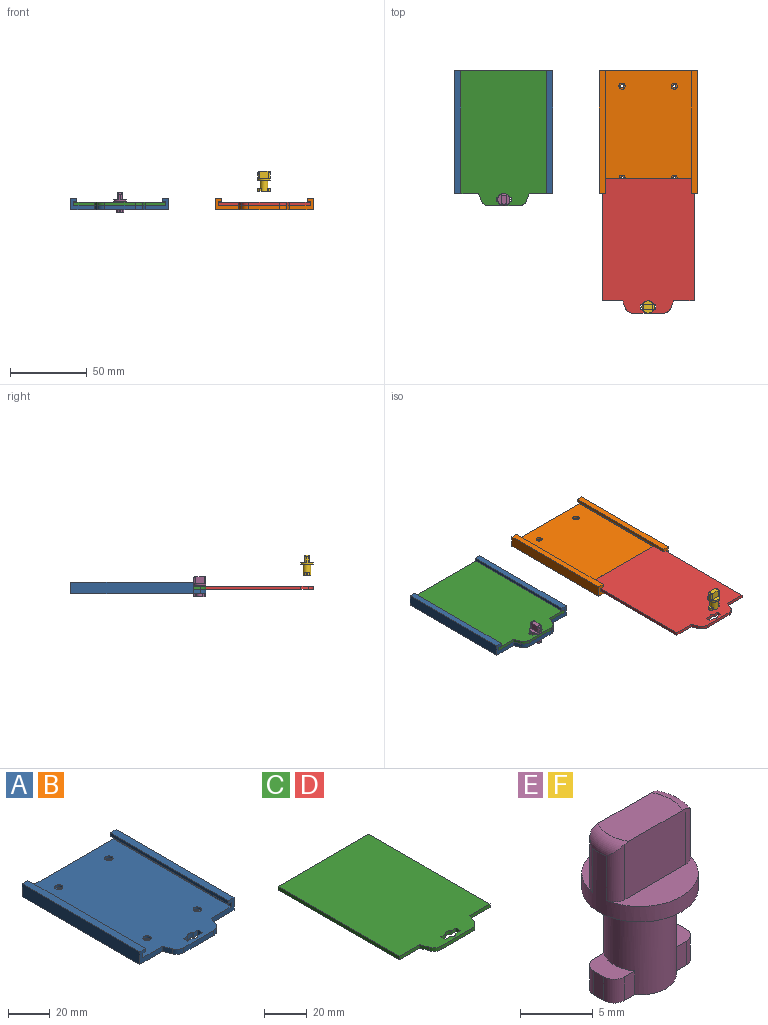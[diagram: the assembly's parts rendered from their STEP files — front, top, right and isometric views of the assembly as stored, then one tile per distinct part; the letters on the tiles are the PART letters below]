
ASSEMBLY  parts=6 mates=4
PART A: 40 faces, bbox 64x88x7.5 mm
  f0: plane 15.5x7.5mm, normal (0,-1,0), area 59.5mm2, adj f3,f4,f5,f6,f7,f8,f9,f29
  f1: plane 80x4mm, normal (0,0,1), area 320mm2, adj f2,f12,f13,f14
  f2: plane 80x7.5mm, normal (-1,0,0), area 600mm2, adj f1,f3,f13,f14
  f3: plane 88x64mm, normal (0,0,-1), area 5307.5mm2, adj f0,f2,f4,f13,f14,f15,f18,f21
  f4: plane 80x7.5mm, normal (1,0,0), area 600mm2, adj f0,f3,f5,f13
  f5: plane 80x4mm, normal (0,0,1), area 320mm2, adj f0,f4,f6,f13
  f6: plane 80x2mm, normal (-1,0,0), area 160mm2, adj f0,f5,f7,f13
  f7: plane 80x2mm, normal (0,0,-1), area 160mm2, adj f0,f6,f8,f13
  f8: plane 80x2.5mm, normal (-1,0,0), area 200mm2, adj f0,f7,f9,f13
  f9: plane 88x60mm, normal (0,0,1), area 4949.8mm2, adj f0,f8,f10,f13,f14,f17,f20,f23
  f10: plane 80x2.5mm, normal (1,0,0), area 200mm2, adj f9,f11,f13,f14
  f11: plane 80x2mm, normal (0,0,-1), area 160mm2, adj f10,f12,f13,f14
  f12: plane 80x2mm, normal (1,0,0), area 160mm2, adj f1,f11,f13,f14
  f13: plane 64x7.5mm, normal (0,1,0), area 218mm2, adj f1,f2,f3,f4,f5,f6,f7,f8
  f14: plane 15.5x7.5mm, normal (0,-1,0), area 59.5mm2, adj f1,f2,f3,f9,f10,f11,f12,f27
  f15: cylinder r=1mm len=2mm, axis (0,0,1), area 9.4mm2, adj f3,f16
  f16: plane 4x4mm, normal (0,0,1), area 9.4mm2, adj f15,f17
  f17: cylinder r=2mm len=4mm, axis (0,0,1), area 18.8mm2, adj f9,f16
  f18: cylinder r=1mm len=2mm, axis (0,0,1), area 9.4mm2, adj f3,f19
  f19: plane 4x4mm, normal (0,0,1), area 9.4mm2, adj f18,f20
  f20: cylinder r=2mm len=4mm, axis (0,0,1), area 18.8mm2, adj f9,f19
  f21: cylinder r=1mm len=2mm, axis (0,0,1), area 9.4mm2, adj f3,f22
  f22: plane 4x4mm, normal (0,0,1), area 9.4mm2, adj f21,f23
  f23: cylinder r=2mm len=4mm, axis (0,0,1), area 18.8mm2, adj f9,f22
  f24: cylinder r=1mm len=2mm, axis (0,0,1), area 9.4mm2, adj f3,f25
  f25: plane 4x4mm, normal (0,0,1), area 9.4mm2, adj f24,f26
  f26: cylinder r=2mm len=4mm, axis (0,0,1), area 18.8mm2, adj f9,f25
  f27: plane 4.76x3mm, normal (-0.94,-0.35,0), area 15.2mm2, adj f3,f9,f14,f38
  f28: plane 20.07x3mm, normal (0,-1,0), area 60.2mm2, adj f3,f9,f38,f39
  f29: plane 4.76x3mm, normal (0.94,-0.35,0), area 15.2mm2, adj f0,f3,f9,f39
  f30: plane 3x3mm, normal (0,1,0), area 9mm2, adj f3,f9,f31,f37
  f31: cylinder r=2.5mm len=4mm, axis (0,0,1), area 13.9mm2, adj f3,f9,f30,f32
  f32: plane 3x3mm, normal (0,1,0), area 9mm2, adj f3,f9,f31,f33
  f33: plane 3x3mm, normal (-1,0,0), area 9mm2, adj f3,f9,f32,f34
  f34: plane 3x3mm, normal (0,-1,0), area 9mm2, adj f3,f9,f33,f35
  f35: cylinder r=2.5mm len=4mm, axis (0,0,1), area 13.9mm2, adj f3,f9,f34,f36
  f36: plane 3x3mm, normal (0,-1,0), area 9mm2, adj f3,f9,f35,f37
  f37: plane 3x3mm, normal (1,0,0), area 9mm2, adj f3,f9,f30,f36
  f38: cylinder r=5mm len=4.68mm, axis (0,0,-1), area 18.2mm2, adj f3,f9,f27,f28
  f39: cylinder r=5mm len=4.68mm, axis (0,0,-1), area 18.2mm2, adj f3,f9,f28,f29
PART B: same geometry as A
PART C: 20 faces, bbox 60x88x2 mm
  f0: plane 13.5x2mm, normal (0,-1,0), area 27mm2, adj f1,f2,f4,f9
  f1: plane 80x2mm, normal (1,0,0), area 160mm2, adj f0,f2,f4,f5
  f2: plane 88x60mm, normal (0,0,1), area 5000.1mm2, adj f0,f1,f3,f5,f6,f7,f8,f9
  f3: plane 80x2mm, normal (-1,0,0), area 160mm2, adj f2,f4,f5,f6
  f4: plane 88x60mm, normal (0,0,-1), area 5000.1mm2, adj f0,f1,f3,f5,f6,f7,f8,f9
  f5: plane 60x2mm, normal (0,1,0), area 120mm2, adj f1,f2,f3,f4
  f6: plane 13.5x2mm, normal (0,-1,0), area 27mm2, adj f2,f3,f4,f7
  f7: plane 4.76x2mm, normal (-0.94,-0.35,0), area 10.2mm2, adj f2,f4,f6,f18
  f8: plane 20.07x2mm, normal (0,-1,0), area 40.1mm2, adj f2,f4,f18,f19
  f9: plane 4.76x2mm, normal (0.94,-0.35,0), area 10.2mm2, adj f0,f2,f4,f19
  f10: plane 3x2mm, normal (0,1,0), area 6mm2, adj f2,f4,f11,f17
  f11: cylinder r=2.5mm len=4mm, axis (0,0,1), area 9.3mm2, adj f2,f4,f10,f12
  f12: plane 3x2mm, normal (0,1,0), area 6mm2, adj f2,f4,f11,f13
  f13: plane 3x2mm, normal (-1,0,0), area 6mm2, adj f2,f4,f12,f14
  f14: plane 3x2mm, normal (0,-1,0), area 6mm2, adj f2,f4,f13,f15
  f15: cylinder r=2.5mm len=4mm, axis (0,0,1), area 9.3mm2, adj f2,f4,f14,f16
  f16: plane 3x2mm, normal (0,-1,0), area 6mm2, adj f2,f4,f15,f17
  f17: plane 3x2mm, normal (1,0,0), area 6mm2, adj f2,f4,f10,f16
  f18: cylinder r=5mm len=4.68mm, axis (0,0,-1), area 12.1mm2, adj f2,f4,f7,f8
  f19: cylinder r=5mm len=4.68mm, axis (0,0,-1), area 12.1mm2, adj f2,f4,f8,f9
PART D: same geometry as C
PART E: 27 faces, bbox 8.7x8x13.2 mm
  f0: cylinder r=4mm len=8mm, axis (0,0,1), area 42.6mm2, adj f12,f13,f15,f17,f18,f19,f20,f21
  f1: plane 6x3mm, normal (0,0,1), area 17.2mm2, adj f14,f16,f18,f21
  f2: cylinder r=2.5mm len=7.2mm, axis (0,0,-1), area 100.3mm2, adj f3,f5,f6,f7,f8,f9,f10,f12
  f3: plane 8x5mm, normal (0,0,-1), area 28.7mm2, adj f2,f4,f6,f7,f9,f10,f11,f23
  f4: plane 2x0.98mm, normal (1,0,0), area 2mm2, adj f3,f5,f25,f26
  f5: plane 2.98x1.99mm, normal (0,0,1), area 4.5mm2, adj f2,f4,f6,f7,f25,f26
  f6: plane 2x0.99mm, normal (0,-1,0), area 2mm2, adj f2,f3,f5,f25
  f7: plane 2x0.99mm, normal (0,1,0), area 2mm2, adj f2,f3,f5,f26
  f8: plane 2.98x1.99mm, normal (0,0,1), area 4.5mm2, adj f2,f9,f10,f11,f23,f24
  f9: plane 2x0.99mm, normal (0,1,0), area 2mm2, adj f2,f3,f8,f23
  f10: plane 2x0.99mm, normal (0,-1,0), area 2mm2, adj f2,f3,f8,f24
  f11: plane 2x0.98mm, normal (-1,0,0), area 2mm2, adj f3,f8,f23,f24
  f12: plane 8x8mm, normal (0,0,-1), area 30.6mm2, adj f0,f2
  f13: plane 7.89x3.33mm, normal (0,0,1), area 13.7mm2, adj f0,f14,f17,f20
  f14: plane 5.93x4.71mm, normal (0,-1,0), area 27.8mm2, adj f1,f13,f17,f18,f20,f21
  f15: plane 7.89x3.33mm, normal (0,0,1), area 13.7mm2, adj f0,f16,f19,f22
  f16: plane 5.93x4.71mm, normal (0,1,0), area 27.8mm2, adj f1,f15,f18,f19,f21,f22
  f17: cylinder r=1mm len=4.65mm, axis (0,0,1), area 6mm2, adj f0,f13,f14,f18
  f18: torus R=3mm, axis (0,0,1), area 4.1mm2, adj f0,f1,f14,f16,f17,f19
  f19: cylinder r=1mm len=4.65mm, axis (0,0,1), area 6mm2, adj f0,f15,f16,f18
  f20: cylinder r=1mm len=4.65mm, axis (0,0,1), area 6mm2, adj f0,f13,f14,f21
  f21: torus R=3mm, axis (0,0,1), area 4.1mm2, adj f0,f1,f14,f16,f20,f22
  f22: cylinder r=1mm len=4.65mm, axis (0,0,1), area 6mm2, adj f0,f15,f16,f21
  f23: cylinder r=1mm len=2mm, axis (0,0,1), area 3.1mm2, adj f3,f8,f9,f11
  f24: cylinder r=1mm len=2mm, axis (0,0,-1), area 3.1mm2, adj f3,f8,f10,f11
  f25: cylinder r=1mm len=2mm, axis (0,0,1), area 3.1mm2, adj f3,f4,f5,f6
  f26: cylinder r=1mm len=2mm, axis (0,0,-1), area 3.1mm2, adj f3,f4,f5,f7
PART F: same geometry as E
PLACE A t=(-47,0,0)mm fixed
PLACE B t=(47,0,0)mm fixed
PLACE C t=(-47,0,3)mm
PLACE D t=(47,-70,3)mm
PLACE E rot(axis=(0,0,-1),90deg) t=(-47,-4,-2)mm
PLACE F rot(axis=(0,0,-1),180deg) t=(47,-74,12)mm
MATE fastened C.f5 <-> A.f13  axis (0,1,0) through (-47,80,3)mm
MATE fastened E.f0 <-> A.f31  axis (0,0,1) through (-47,-4,0)mm
MATE slider D.f6 <-> B.f14  axis (0,-1,0) through (17,-70,3)mm
MATE cylindrical F.f0 <-> D.f11  axis (0,0,-1) through (47,-74,12)mm
